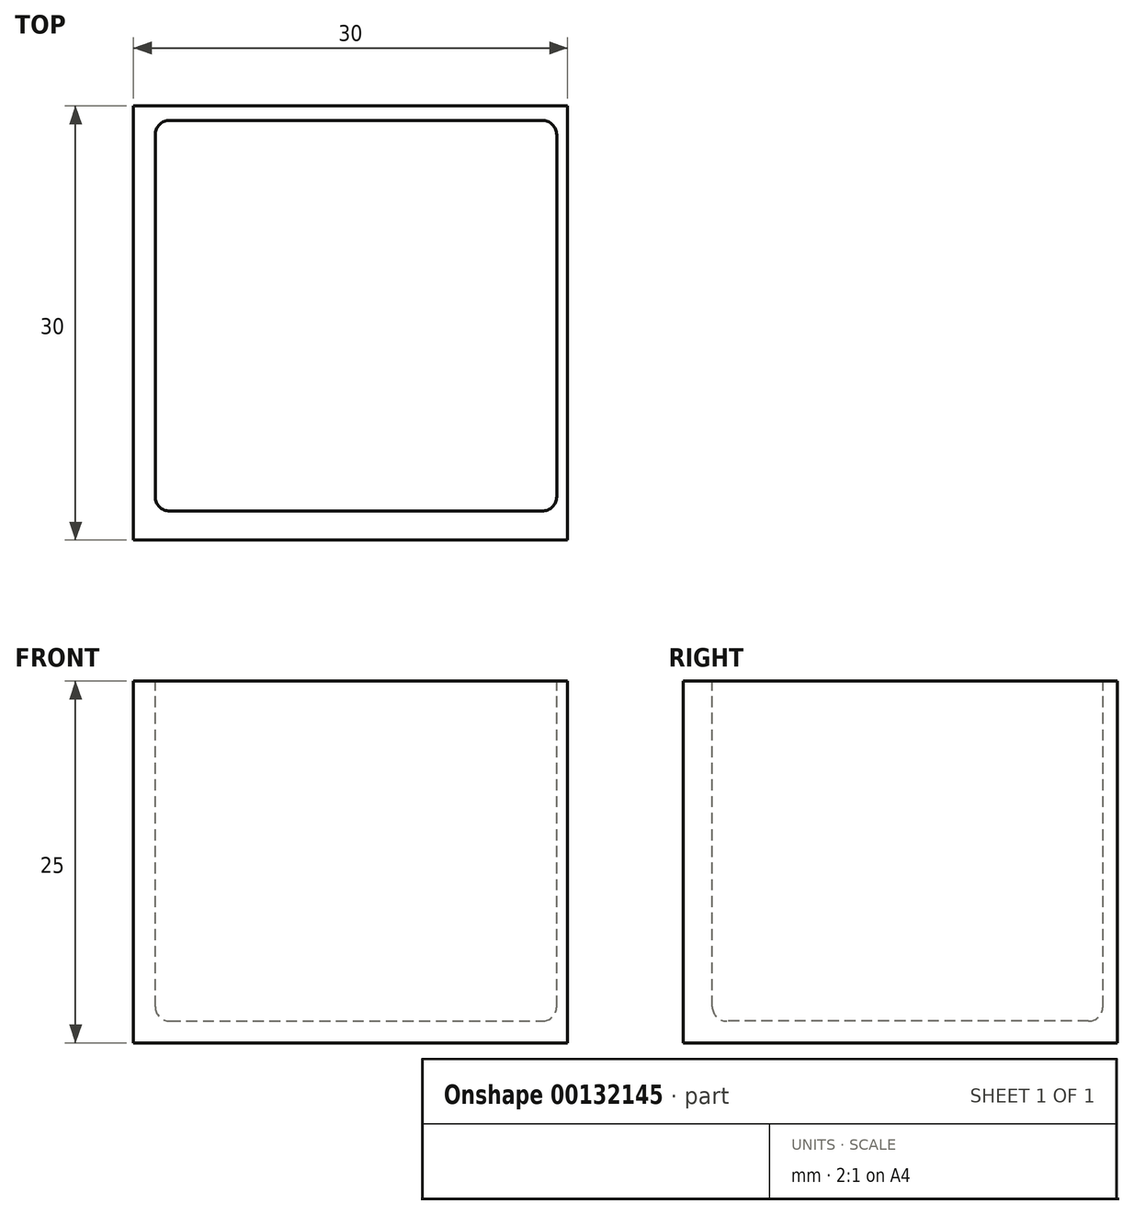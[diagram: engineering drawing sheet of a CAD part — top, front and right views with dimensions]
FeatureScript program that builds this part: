
annotation { "Feature Type Name" : "Feature", "Feature Type Description" : "" }
export const myFeature = defineFeature(function(context is Context, id is Id, definition is map)
    precondition{}
    {
        {
            var Q0;
            Q0=qCreatedBy(makeId("Top.planeOp"),FACE);
            var sketch = newSketch(context, id + "F0", { "sketchPlane" : qUnion([Q0])});
            skLineSegment(sketch, "E0.bottom", {"start": v(-13.65, -24.67) * mm, "end": v(16.35, -24.67) * mm});
            skLineSegment(sketch, "E0.top", {"start": v(-13.65, 5.33) * mm, "end": v(16.35, 5.33) * mm});
            skLineSegment(sketch, "E0.left", {"start": v(-13.65, -24.67) * mm, "end": v(-13.65, 5.33) * mm});
            skLineSegment(sketch, "E0.right", {"start": v(16.35, -24.67) * mm, "end": v(16.35, 5.33) * mm});
            skSolve(sketch);
        }
        {
            var Q0;
            Q0=makeQuery(id+"F0.imprint","IMPRINT",FACE,{"disambiguationData":[TD([[makeQuery(id+"F0.imprint","IMPRINT",EDGE,{"derivedFrom":sQuery(id+"F0.wireOp",EDGE,"E0.bottom")}),1.0]])]});
            extrude(context, id + "F1", {"entities" : qUnion([Q0]), "depth" : 25 * mm});
        }
        {
            var Q0;
            Q0=makeQuery(id+"F1.opExtrude","CAP_FACE",FACE,{"disambiguationData":[OSD([sQuery(id+"F0.wireOp",EDGE,"E0.bottom"),sQuery(id+"F0.wireOp",EDGE,"E0.top"),sQuery(id+"F0.wireOp",EDGE,"E0.left"),sQuery(id+"F0.wireOp",EDGE,"E0.right")])],"isStart":false});
            var sketch = newSketch(context, id + "F2", { "sketchPlane" : qUnion([Q0])});
            skLineSegment(sketch, "E1.bottom", {"start": v(-12.15, 4.33) * mm, "end": v(15.6, 4.33) * mm});
            skLineSegment(sketch, "E1.top", {"start": v(-12.15, -22.67) * mm, "end": v(15.6, -22.67) * mm});
            skLineSegment(sketch, "E1.left", {"start": v(-12.15, 4.33) * mm, "end": v(-12.15, -22.67) * mm});
            skLineSegment(sketch, "E1.right", {"start": v(15.6, 4.33) * mm, "end": v(15.6, -22.67) * mm});
            skSolve(sketch);
        }
        {
            var Q0;
            Q0=makeQuery(id+"F2.imprint","IMPRINT",FACE,{"disambiguationData":[TD([[makeQuery(id+"F2.imprint","IMPRINT",EDGE,{"derivedFrom":sQuery(id+"F2.wireOp",EDGE,"E1.bottom")}),-1.0]])]});
            extrude(context, id + "F3", {"entities" : qUnion([Q0]), "operationType" : NewBodyOperationType.REMOVE, "oppositeDirection" : true, "depth" : 23.5 * mm});
        }
        {
            var Q0;
            Q0=makeQuery(id+"F3.boolean.opBoolean","COPY",EDGE,{"derivedFrom":makeQuery(id+"F3.opExtrude","SWEPT_EDGE",EDGE,{"disambiguationData":[OSD([sQuery(id+"F2.wireOp",EDGE,"E1.bottom"),sQuery(id+"F2.wireOp",EDGE,"E1.left")])]})});
            var Q1;
            Q1=makeQuery(id+"F3.boolean.opBoolean","COPY",EDGE,{"derivedFrom":makeQuery(id+"F3.opExtrude","CAP_EDGE",EDGE,{"disambiguationData":[OSD([sQuery(id+"F2.wireOp",EDGE,"E1.left")])],"isStart":false})});
            var Q2;
            Q2=makeQuery(id+"F3.boolean.opBoolean","COPY",EDGE,{"derivedFrom":makeQuery(id+"F3.opExtrude","CAP_EDGE",EDGE,{"disambiguationData":[OSD([sQuery(id+"F2.wireOp",EDGE,"E1.bottom")])],"isStart":false})});
            var Q3;
            Q3=makeQuery(id+"F3.boolean.opBoolean","COPY",EDGE,{"derivedFrom":makeQuery(id+"F3.opExtrude","SWEPT_EDGE",EDGE,{"disambiguationData":[OSD([sQuery(id+"F2.wireOp",EDGE,"E1.bottom"),sQuery(id+"F2.wireOp",EDGE,"E1.right")])]})});
            var Q4;
            Q4=makeQuery(id+"F3.boolean.opBoolean","COPY",EDGE,{"derivedFrom":makeQuery(id+"F3.opExtrude","CAP_EDGE",EDGE,{"disambiguationData":[OSD([sQuery(id+"F2.wireOp",EDGE,"E1.right")])],"isStart":false})});
            var Q5;
            Q5=makeQuery(id+"F3.boolean.opBoolean","COPY",EDGE,{"derivedFrom":makeQuery(id+"F3.opExtrude","CAP_EDGE",EDGE,{"disambiguationData":[OSD([sQuery(id+"F2.wireOp",EDGE,"E1.top")])],"isStart":false})});
            var Q6;
            Q6=makeQuery(id+"F3.boolean.opBoolean","COPY",EDGE,{"derivedFrom":makeQuery(id+"F3.opExtrude","SWEPT_EDGE",EDGE,{"disambiguationData":[OSD([sQuery(id+"F2.wireOp",EDGE,"E1.top"),sQuery(id+"F2.wireOp",EDGE,"E1.right")])]})});
            var Q7;
            Q7=makeQuery(id+"F3.boolean.opBoolean","COPY",EDGE,{"derivedFrom":makeQuery(id+"F3.opExtrude","SWEPT_EDGE",EDGE,{"disambiguationData":[OSD([sQuery(id+"F2.wireOp",EDGE,"E1.top"),sQuery(id+"F2.wireOp",EDGE,"E1.left")])]})});
            fillet(context, id + "F4", {"entities" : qUnion([Q0, Q1, Q2, Q3, Q4, Q5, Q6, Q7]), "radius" : 1 * mm, "tangentPropagation" : true, "allowEdgeOverflow" : false});
        }
    });
